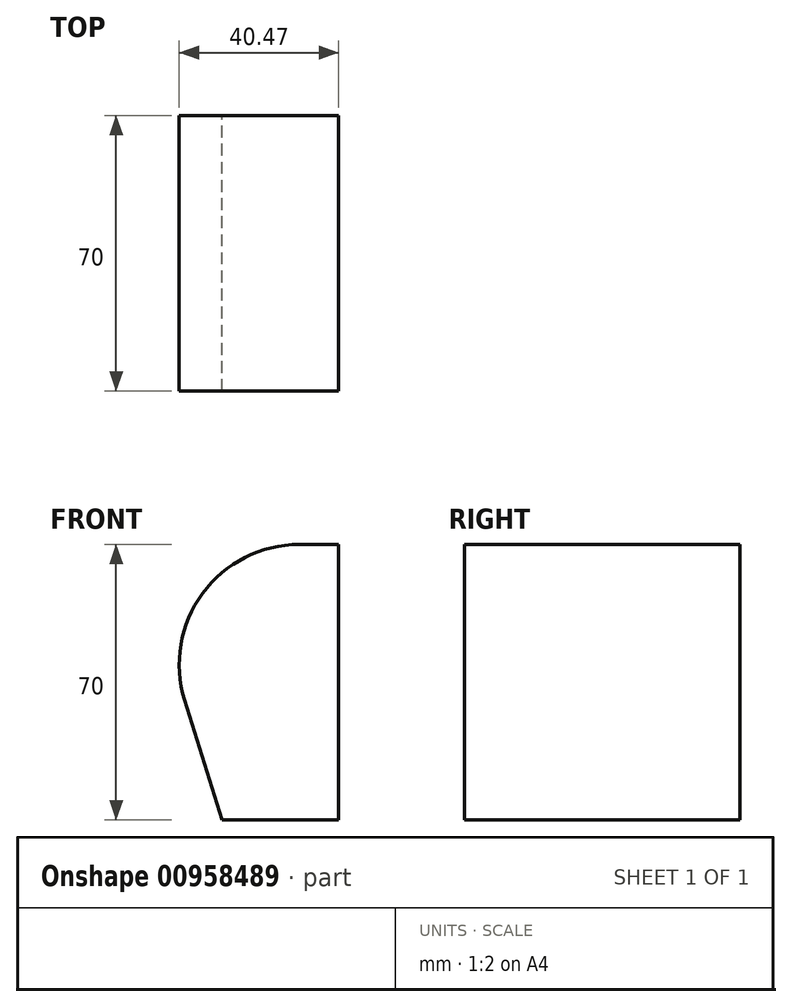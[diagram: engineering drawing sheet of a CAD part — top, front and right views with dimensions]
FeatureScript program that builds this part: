
annotation { "Feature Type Name" : "Feature", "Feature Type Description" : "" }
export const myFeature = defineFeature(function(context is Context, id is Id, definition is map)
    precondition{}
    {
        {
            var Q0;
            Q0=qCreatedBy(makeId("Front.planeOp"),FACE);
            var sketch = newSketch(context, id + "F0", { "sketchPlane" : qUnion([Q0])});
            skLineSegment(sketch, "E0", {"start": v(-196.9, 16.45) * mm, "end": v(-187.4, -14) * mm});
            skLineSegment(sketch, "E1", {"start": v(-167.8, 56) * mm, "end": v(-157.8, 56) * mm});
            skArc(sketch, "E2", {"start": v(-167.8, 56) * mm, "mid": v(-192.35, 43.58) * mm, "end": v(-196.9, 16.45) * mm});
            skLineSegment(sketch, "E3", {"start": v(-157.8, 56) * mm, "end": v(-157.8, -14) * mm});
            skLineSegment(sketch, "E4", {"start": v(-157.8, -14) * mm, "end": v(-187.4, -14) * mm});
            skSolve(sketch);
        }
        {
            var Q0;
            Q0=makeQuery(id+"F0.imprint","IMPRINT",FACE,{"disambiguationData":[TD([[makeQuery(id+"F0.imprint","IMPRINT",EDGE,{"derivedFrom":sQuery(id+"F0.wireOp",EDGE,"E0")}),1.0]])]});
            extrude(context, id + "F1", {"entities" : qUnion([Q0]), "endBound" : BoundingType.SYMMETRIC, "depth" : 70 * mm, "offsetDistance" : 25 * mm});
        }
    });
